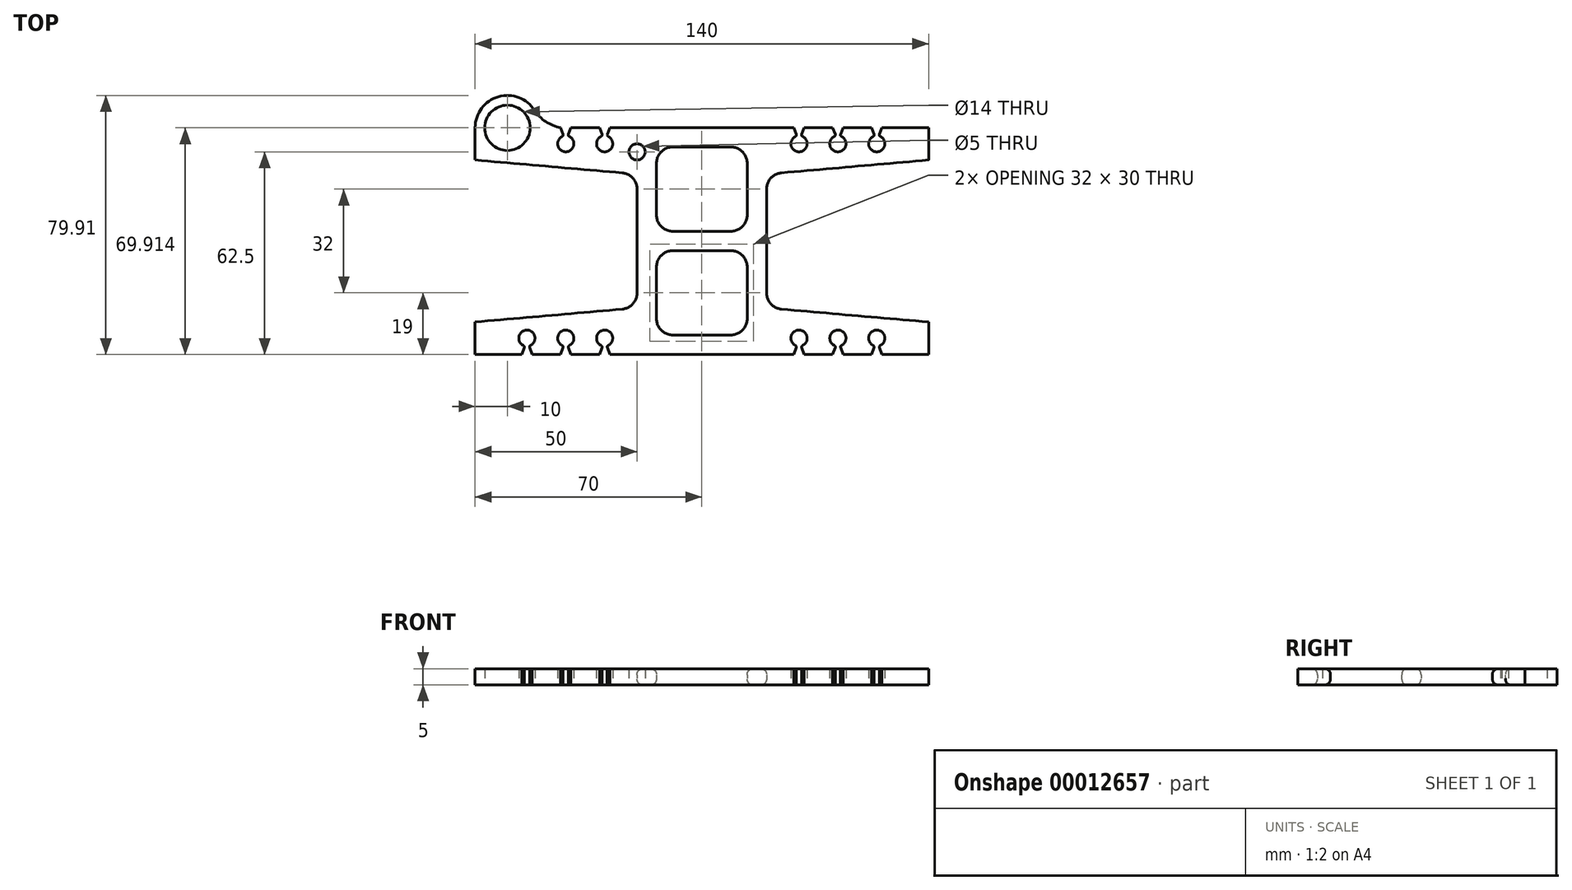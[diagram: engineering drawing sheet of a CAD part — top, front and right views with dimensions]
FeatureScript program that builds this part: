
annotation { "Feature Type Name" : "Feature", "Feature Type Description" : "" }
export const myFeature = defineFeature(function(context is Context, id is Id, definition is map)
    precondition{}
    {
        {
            var Q0;
            Q0=qCreatedBy(makeId("Top.planeOp"),FACE);
            var sketch = newSketch(context, id + "F0", { "sketchPlane" : qUnion([Q0])});
            skLineSegment(sketch, "E0", {"start": v(-20, -16.04) * mm, "end": v(-20, 16.04) * mm});
            skLineSegment(sketch, "E1", {"start": v(-24.56, 21.02) * mm, "end": v(-70, 25) * mm});
            skLineSegment(sketch, "E2", {"start": v(-70, 25) * mm, "end": v(-70, 35) * mm});
            skLineSegment(sketch, "E3", {"start": v(0, 0) * mm, "end": v(-9.78, 0) * mm, "construction": true});
            skLineSegment(sketch, "E4.0.MirrorCS", {"start": v(-70, -25) * mm, "end": v(-70, -35) * mm});
            skLineSegment(sketch, "E5", {"start": v(0, 0) * mm, "end": v(0, 8.93) * mm, "construction": true});
            skLineSegment(sketch, "E6.0.MirrorCS", {"start": v(70, 25) * mm, "end": v(70, 35) * mm});
            skLineSegment(sketch, "E7.0.MirrorCS", {"start": v(70, -25) * mm, "end": v(70, -35) * mm});
            skLineSegment(sketch, "E8", {"start": v(-70, 35) * mm, "end": v(70, 35) * mm});
            skLineSegment(sketch, "E9", {"start": v(-70, -35) * mm, "end": v(70, -35) * mm});
            skPoint(sketch, "E10.visualSharp", {"position": v(-20, 0) * mm});
            skPoint(sketch, "E11.visualSharp", {"position": v(-20, 20.63) * mm});
            skArc(sketch, "E11.filletArc", {"start": v(-20, 16.04) * mm, "mid": v(-21.31, 19.42) * mm, "end": v(-24.56, 21.02) * mm});
            skLineSegment(sketch, "E12.0.MirrorCS", {"start": v(-20, 16.04) * mm, "end": v(-20, -16.04) * mm});
            skArc(sketch, "E13.0.MirrorCS", {"start": v(-20, -16.04) * mm, "mid": v(-21.31, -19.42) * mm, "end": v(-24.56, -21.02) * mm});
            skLineSegment(sketch, "E14.0.MirrorCS", {"start": v(-24.56, -21.02) * mm, "end": v(-70, -25) * mm});
            skLineSegment(sketch, "E15.0.MirrorCS", {"start": v(24.56, 21.02) * mm, "end": v(70, 25) * mm});
            skArc(sketch, "E16.0.MirrorCS", {"start": v(20, 16.04) * mm, "mid": v(21.31, 19.42) * mm, "end": v(24.56, 21.02) * mm});
            skLineSegment(sketch, "E17.0.MirrorCS", {"start": v(20, -16.04) * mm, "end": v(20, 16.04) * mm});
            skLineSegment(sketch, "E18.0.MirrorCS", {"start": v(20, 16.04) * mm, "end": v(20, -16.04) * mm});
            skArc(sketch, "E19.0.MirrorCS", {"start": v(20, -16.04) * mm, "mid": v(21.31, -19.42) * mm, "end": v(24.56, -21.02) * mm});
            skLineSegment(sketch, "E20.0.MirrorCS", {"start": v(24.56, -21.02) * mm, "end": v(70, -25) * mm});
            skLineSegment(sketch, "E21", {"start": v(-14, 8) * mm, "end": v(-14, 24) * mm});
            skLineSegment(sketch, "E22", {"start": v(-9, 29) * mm, "end": v(9, 29) * mm});
            skLineSegment(sketch, "E23.0.MirrorCS", {"start": v(14, 8) * mm, "end": v(14, 24) * mm});
            skLineSegment(sketch, "E24.0.MirrorCS", {"start": v(-14, -8) * mm, "end": v(-14, -24) * mm});
            skLineSegment(sketch, "E25.0.MirrorCS", {"start": v(-9, -29) * mm, "end": v(9, -29) * mm});
            skLineSegment(sketch, "E26.0.MirrorCS", {"start": v(14, -8) * mm, "end": v(14, -24) * mm});
            skPoint(sketch, "E27.visualSharp", {"position": v(-14, 29) * mm});
            skArc(sketch, "E27.filletArc", {"start": v(-9, 29) * mm, "mid": v(-12.54, 27.54) * mm, "end": v(-14, 24) * mm});
            skPoint(sketch, "E28.visualSharp", {"position": v(14, 29) * mm});
            skArc(sketch, "E28.filletArc", {"start": v(14, 24) * mm, "mid": v(12.54, 27.54) * mm, "end": v(9, 29) * mm});
            skPoint(sketch, "E29.visualSharp", {"position": v(-14, -29) * mm});
            skArc(sketch, "E29.filletArc", {"start": v(-14, -24) * mm, "mid": v(-12.54, -27.54) * mm, "end": v(-9, -29) * mm});
            skPoint(sketch, "E30.visualSharp", {"position": v(14, -29) * mm});
            skArc(sketch, "E30.filletArc", {"start": v(9, -29) * mm, "mid": v(12.54, -27.54) * mm, "end": v(14, -24) * mm});
            skLineSegment(sketch, "E31", {"start": v(-9, 3) * mm, "end": v(9, 3) * mm});
            skLineSegment(sketch, "E32.0.MirrorCS", {"start": v(-9, -3) * mm, "end": v(9, -3) * mm});
            skPoint(sketch, "E33.orphan", {"position": v(-14, 0) * mm});
            skPoint(sketch, "E34.orphan", {"position": v(14, 0) * mm});
            skPoint(sketch, "E35.visualSharp", {"position": v(-14, 3) * mm});
            skArc(sketch, "E35.filletArc", {"start": v(-14, 8) * mm, "mid": v(-12.54, 4.46) * mm, "end": v(-9, 3) * mm});
            skPoint(sketch, "E36.visualSharp", {"position": v(14, 3) * mm});
            skArc(sketch, "E36.filletArc", {"start": v(9, 3) * mm, "mid": v(12.54, 4.46) * mm, "end": v(14, 8) * mm});
            skPoint(sketch, "E37.visualSharp", {"position": v(-14, -3) * mm});
            skArc(sketch, "E37.filletArc", {"start": v(-9, -3) * mm, "mid": v(-12.54, -4.46) * mm, "end": v(-14, -8) * mm});
            skPoint(sketch, "E38.visualSharp", {"position": v(14, -3) * mm});
            skArc(sketch, "E38.filletArc", {"start": v(14, -8) * mm, "mid": v(12.54, -4.46) * mm, "end": v(9, -3) * mm});
            skSolve(sketch);
        }
        {
            var Q0;
            Q0 = qSketchRegion(id + "F0", true);
            extrude(context, id + "F1", {"entities" : qUnion([Q0]), "depth" : 5 * mm});
        }
        {
            var Q0;
            Q0=qCreatedBy(makeId("Top.planeOp"),FACE);
            var sketch = newSketch(context, id + "F2", { "sketchPlane" : qUnion([Q0])});
            skLineSegment(sketch, "E39", {"start": v(-32.08, -36.31) * mm, "end": v(-30.83, -32.87) * mm});
            skLineSegment(sketch, "E40", {"start": v(-30, -26.33) * mm, "end": v(-30, -30) * mm, "construction": true});
            skArc(sketch, "E41", {"start": v(-30, -27.5) * mm, "mid": v(-32.44, -29.44) * mm, "end": v(-31.08, -32.25) * mm});
            skArc(sketch, "E42.filletArc", {"start": v(-30.83, -32.87) * mm, "mid": v(-30.84, -32.52) * mm, "end": v(-31.08, -32.25) * mm});
            skLineSegment(sketch, "E43.0.MirrorCS", {"start": v(-27.92, -36.31) * mm, "end": v(-29.17, -32.87) * mm});
            skArc(sketch, "E44.0.MirrorCS", {"start": v(-29.17, -32.87) * mm, "mid": v(-29.16, -32.52) * mm, "end": v(-28.92, -32.25) * mm});
            skArc(sketch, "E45.0.MirrorCS", {"start": v(-30, -27.5) * mm, "mid": v(-27.56, -29.44) * mm, "end": v(-28.92, -32.25) * mm});
            skLineSegment(sketch, "E46", {"start": v(-32.08, -36.31) * mm, "end": v(-27.92, -36.31) * mm});
            skLineSegment(sketch, "E47", {"start": v(0, 0) * mm, "end": v(0, -10.66) * mm, "construction": true});
            skArc(sketch, "E48.1.0.0", {"start": v(-42, -27.5) * mm, "mid": v(-44.44, -29.44) * mm, "end": v(-43.08, -32.25) * mm});
            skLineSegment(sketch, "E48.1.0.1", {"start": v(-44.08, -36.31) * mm, "end": v(-39.92, -36.31) * mm});
            skArc(sketch, "E48.1.0.2", {"start": v(-42, -27.5) * mm, "mid": v(-39.56, -29.44) * mm, "end": v(-40.92, -32.25) * mm});
            skLineSegment(sketch, "E48.1.0.3", {"start": v(-39.92, -36.31) * mm, "end": v(-41.17, -32.87) * mm});
            skLineSegment(sketch, "E48.1.0.4", {"start": v(-42, -26.33) * mm, "end": v(-42, -30) * mm, "construction": true});
            skLineSegment(sketch, "E48.1.0.5", {"start": v(-44.08, -36.31) * mm, "end": v(-42.83, -32.87) * mm});
            skArc(sketch, "E48.1.0.6", {"start": v(-41.17, -32.87) * mm, "mid": v(-41.16, -32.52) * mm, "end": v(-40.92, -32.25) * mm});
            skArc(sketch, "E48.1.0.7", {"start": v(-42.83, -32.87) * mm, "mid": v(-42.84, -32.52) * mm, "end": v(-43.08, -32.25) * mm});
            skArc(sketch, "E48.2.0.0", {"start": v(-54, -27.5) * mm, "mid": v(-56.44, -29.44) * mm, "end": v(-55.08, -32.25) * mm});
            skLineSegment(sketch, "E48.2.0.1", {"start": v(-56.08, -36.31) * mm, "end": v(-51.92, -36.31) * mm});
            skArc(sketch, "E48.2.0.2", {"start": v(-54, -27.5) * mm, "mid": v(-51.56, -29.44) * mm, "end": v(-52.92, -32.25) * mm});
            skLineSegment(sketch, "E48.2.0.3", {"start": v(-51.92, -36.31) * mm, "end": v(-53.17, -32.87) * mm});
            skLineSegment(sketch, "E48.2.0.4", {"start": v(-54, -26.33) * mm, "end": v(-54, -30) * mm, "construction": true});
            skLineSegment(sketch, "E48.2.0.5", {"start": v(-56.08, -36.31) * mm, "end": v(-54.83, -32.87) * mm});
            skArc(sketch, "E48.2.0.6", {"start": v(-53.17, -32.87) * mm, "mid": v(-53.16, -32.52) * mm, "end": v(-52.92, -32.25) * mm});
            skArc(sketch, "E48.2.0.7", {"start": v(-54.83, -32.87) * mm, "mid": v(-54.84, -32.52) * mm, "end": v(-55.08, -32.25) * mm});
            skLineSegment(sketch, "E48.direction1", {"start": v(-31.08, -32.25) * mm, "end": v(-43.08, -32.25) * mm, "construction": true});
            skLineSegment(sketch, "E49", {"start": v(0, 0) * mm, "end": v(8.83, 0) * mm, "construction": true});
            skArc(sketch, "E50.0.MirrorCS", {"start": v(30.83, -32.87) * mm, "mid": v(30.84, -32.52) * mm, "end": v(31.08, -32.25) * mm});
            skArc(sketch, "E50.1.MirrorCS", {"start": v(41.17, -32.87) * mm, "mid": v(41.16, -32.52) * mm, "end": v(40.92, -32.25) * mm});
            skArc(sketch, "E50.2.MirrorCS", {"start": v(53.17, -32.87) * mm, "mid": v(53.16, -32.52) * mm, "end": v(52.92, -32.25) * mm});
            skArc(sketch, "E50.3.MirrorCS", {"start": v(42.83, -32.87) * mm, "mid": v(42.84, -32.52) * mm, "end": v(43.08, -32.25) * mm});
            skArc(sketch, "E50.4.MirrorCS", {"start": v(54.83, -32.87) * mm, "mid": v(54.84, -32.52) * mm, "end": v(55.08, -32.25) * mm});
            skArc(sketch, "E50.5.MirrorCS", {"start": v(29.17, -32.87) * mm, "mid": v(29.16, -32.52) * mm, "end": v(28.92, -32.25) * mm});
            skArc(sketch, "E50.6.MirrorCS", {"start": v(30, -27.5) * mm, "mid": v(32.44, -29.44) * mm, "end": v(31.08, -32.25) * mm});
            skLineSegment(sketch, "E50.7.MirrorCS", {"start": v(32.08, -36.31) * mm, "end": v(30.83, -32.87) * mm});
            skLineSegment(sketch, "E50.8.MirrorCS", {"start": v(30, -26.33) * mm, "end": v(30, -30) * mm, "construction": true});
            skLineSegment(sketch, "E50.9.MirrorCS", {"start": v(44.08, -36.31) * mm, "end": v(39.92, -36.31) * mm});
            skArc(sketch, "E50.10.MirrorCS", {"start": v(30, -27.5) * mm, "mid": v(27.56, -29.44) * mm, "end": v(28.92, -32.25) * mm});
            skArc(sketch, "E50.11.MirrorCS", {"start": v(54, -27.5) * mm, "mid": v(56.44, -29.44) * mm, "end": v(55.08, -32.25) * mm});
            skLineSegment(sketch, "E50.12.MirrorCS", {"start": v(44.08, -36.31) * mm, "end": v(42.83, -32.87) * mm});
            skLineSegment(sketch, "E50.13.MirrorCS", {"start": v(42, -26.33) * mm, "end": v(42, -30) * mm, "construction": true});
            skLineSegment(sketch, "E50.14.MirrorCS", {"start": v(31.08, -32.25) * mm, "end": v(43.08, -32.25) * mm, "construction": true});
            skLineSegment(sketch, "E50.15.MirrorCS", {"start": v(54, -26.33) * mm, "end": v(54, -30) * mm, "construction": true});
            skLineSegment(sketch, "E50.16.MirrorCS", {"start": v(56.08, -36.31) * mm, "end": v(51.92, -36.31) * mm});
            skLineSegment(sketch, "E50.17.MirrorCS", {"start": v(27.92, -36.31) * mm, "end": v(29.17, -32.87) * mm});
            skLineSegment(sketch, "E50.18.MirrorCS", {"start": v(56.08, -36.31) * mm, "end": v(54.83, -32.87) * mm});
            skArc(sketch, "E50.19.MirrorCS", {"start": v(42, -27.5) * mm, "mid": v(44.44, -29.44) * mm, "end": v(43.08, -32.25) * mm});
            skArc(sketch, "E50.20.MirrorCS", {"start": v(54, -27.5) * mm, "mid": v(51.56, -29.44) * mm, "end": v(52.92, -32.25) * mm});
            skLineSegment(sketch, "E50.21.MirrorCS", {"start": v(39.92, -36.31) * mm, "end": v(41.17, -32.87) * mm});
            skLineSegment(sketch, "E50.22.MirrorCS", {"start": v(51.92, -36.31) * mm, "end": v(53.17, -32.87) * mm});
            skArc(sketch, "E50.23.MirrorCS", {"start": v(42, -27.5) * mm, "mid": v(39.56, -29.44) * mm, "end": v(40.92, -32.25) * mm});
            skLineSegment(sketch, "E50.24.MirrorCS", {"start": v(32.08, -36.31) * mm, "end": v(27.92, -36.31) * mm});
            skArc(sketch, "E51.0.MirrorCS", {"start": v(42.83, 32.87) * mm, "mid": v(42.84, 32.52) * mm, "end": v(43.08, 32.25) * mm});
            skArc(sketch, "E51.1.MirrorCS", {"start": v(30.83, 32.87) * mm, "mid": v(30.84, 32.52) * mm, "end": v(31.08, 32.25) * mm});
            skArc(sketch, "E51.2.MirrorCS", {"start": v(53.17, 32.87) * mm, "mid": v(53.16, 32.52) * mm, "end": v(52.92, 32.25) * mm});
            skArc(sketch, "E51.3.MirrorCS", {"start": v(54.83, 32.87) * mm, "mid": v(54.84, 32.52) * mm, "end": v(55.08, 32.25) * mm});
            skArc(sketch, "E51.4.MirrorCS", {"start": v(29.17, 32.87) * mm, "mid": v(29.16, 32.52) * mm, "end": v(28.92, 32.25) * mm});
            skArc(sketch, "E51.5.MirrorCS", {"start": v(41.17, 32.87) * mm, "mid": v(41.16, 32.52) * mm, "end": v(40.92, 32.25) * mm});
            skLineSegment(sketch, "E51.6.MirrorCS", {"start": v(39.92, 36.31) * mm, "end": v(41.17, 32.87) * mm});
            skLineSegment(sketch, "E51.7.MirrorCS", {"start": v(56.08, 36.31) * mm, "end": v(51.92, 36.31) * mm});
            skLineSegment(sketch, "E51.8.MirrorCS", {"start": v(44.08, 36.31) * mm, "end": v(42.83, 32.87) * mm});
            skArc(sketch, "E51.9.MirrorCS", {"start": v(30, 27.5) * mm, "mid": v(32.44, 29.44) * mm, "end": v(31.08, 32.25) * mm});
            skLineSegment(sketch, "E51.10.MirrorCS", {"start": v(56.08, 36.31) * mm, "end": v(54.83, 32.87) * mm});
            skArc(sketch, "E51.11.MirrorCS", {"start": v(54, 27.5) * mm, "mid": v(56.44, 29.44) * mm, "end": v(55.08, 32.25) * mm});
            skLineSegment(sketch, "E51.12.MirrorCS", {"start": v(30, 26.33) * mm, "end": v(30, 30) * mm, "construction": true});
            skLineSegment(sketch, "E51.13.MirrorCS", {"start": v(54, 26.33) * mm, "end": v(54, 30) * mm, "construction": true});
            skArc(sketch, "E51.14.MirrorCS", {"start": v(42, 27.5) * mm, "mid": v(39.56, 29.44) * mm, "end": v(40.92, 32.25) * mm});
            skArc(sketch, "E51.15.MirrorCS", {"start": v(54, 27.5) * mm, "mid": v(51.56, 29.44) * mm, "end": v(52.92, 32.25) * mm});
            skArc(sketch, "E51.16.MirrorCS", {"start": v(42, 27.5) * mm, "mid": v(44.44, 29.44) * mm, "end": v(43.08, 32.25) * mm});
            skLineSegment(sketch, "E51.17.MirrorCS", {"start": v(51.92, 36.31) * mm, "end": v(53.17, 32.87) * mm});
            skLineSegment(sketch, "E51.18.MirrorCS", {"start": v(32.08, 36.31) * mm, "end": v(30.83, 32.87) * mm});
            skLineSegment(sketch, "E51.19.MirrorCS", {"start": v(27.92, 36.31) * mm, "end": v(29.17, 32.87) * mm});
            skLineSegment(sketch, "E51.20.MirrorCS", {"start": v(44.08, 36.31) * mm, "end": v(39.92, 36.31) * mm});
            skLineSegment(sketch, "E51.21.MirrorCS", {"start": v(42, 26.33) * mm, "end": v(42, 30) * mm, "construction": true});
            skLineSegment(sketch, "E51.22.MirrorCS", {"start": v(31.08, 32.25) * mm, "end": v(43.08, 32.25) * mm, "construction": true});
            skLineSegment(sketch, "E51.23.MirrorCS", {"start": v(32.08, 36.31) * mm, "end": v(27.92, 36.31) * mm});
            skArc(sketch, "E51.24.MirrorCS", {"start": v(30, 27.5) * mm, "mid": v(27.56, 29.44) * mm, "end": v(28.92, 32.25) * mm});
            skArc(sketch, "E52.0.MirrorCS", {"start": v(-30.83, 32.87) * mm, "mid": v(-30.84, 32.52) * mm, "end": v(-31.08, 32.25) * mm});
            skArc(sketch, "E52.1.MirrorCS", {"start": v(-29.17, 32.87) * mm, "mid": v(-29.16, 32.52) * mm, "end": v(-28.92, 32.25) * mm});
            skArc(sketch, "E52.2.MirrorCS", {"start": v(-42.83, 32.87) * mm, "mid": v(-42.84, 32.52) * mm, "end": v(-43.08, 32.25) * mm});
            skLineSegment(sketch, "E52.3.MirrorCS", {"start": v(-30, 26.33) * mm, "end": v(-30, 30) * mm, "construction": true});
            skLineSegment(sketch, "E52.4.MirrorCS", {"start": v(-31.08, 32.25) * mm, "end": v(-43.08, 32.25) * mm, "construction": true});
            skLineSegment(sketch, "E52.5.MirrorCS", {"start": v(-42, 26.33) * mm, "end": v(-42, 30) * mm, "construction": true});
            skArc(sketch, "E52.6.MirrorCS", {"start": v(-41.17, 32.87) * mm, "mid": v(-41.16, 32.52) * mm, "end": v(-40.92, 32.25) * mm});
            skLineSegment(sketch, "E52.7.MirrorCS", {"start": v(-32.08, 36.31) * mm, "end": v(-27.92, 36.31) * mm});
            skArc(sketch, "E52.8.MirrorCS", {"start": v(-30, 27.5) * mm, "mid": v(-32.44, 29.44) * mm, "end": v(-31.08, 32.25) * mm});
            skArc(sketch, "E52.9.MirrorCS", {"start": v(-30, 27.5) * mm, "mid": v(-27.56, 29.44) * mm, "end": v(-28.92, 32.25) * mm});
            skLineSegment(sketch, "E52.10.MirrorCS", {"start": v(-39.92, 36.31) * mm, "end": v(-41.17, 32.87) * mm});
            skLineSegment(sketch, "E52.11.MirrorCS", {"start": v(-44.08, 36.31) * mm, "end": v(-39.92, 36.31) * mm});
            skLineSegment(sketch, "E52.12.MirrorCS", {"start": v(-32.08, 36.31) * mm, "end": v(-30.83, 32.87) * mm});
            skLineSegment(sketch, "E52.13.MirrorCS", {"start": v(-27.92, 36.31) * mm, "end": v(-29.17, 32.87) * mm});
            skArc(sketch, "E52.14.MirrorCS", {"start": v(-42, 27.5) * mm, "mid": v(-39.56, 29.44) * mm, "end": v(-40.92, 32.25) * mm});
            skLineSegment(sketch, "E52.15.MirrorCS", {"start": v(-44.08, 36.31) * mm, "end": v(-42.83, 32.87) * mm});
            skArc(sketch, "E52.16.MirrorCS", {"start": v(-42, 27.5) * mm, "mid": v(-44.44, 29.44) * mm, "end": v(-43.08, 32.25) * mm});
            skSolve(sketch);
        }
        {
            var Q0;
            Q0 = qSketchRegion(id + "F2", true);
            extrude(context, id + "F3", {"entities" : qUnion([Q0]), "operationType" : NewBodyOperationType.REMOVE, "endBound" : BoundingType.THROUGH_ALL, "depth" : 25 * mm});
        }
        {
            var Q0;
            Q0=qCreatedBy(makeId("Top.planeOp"),FACE);
            var sketch = newSketch(context, id + "F4", { "sketchPlane" : qUnion([Q0])});
            skCircle(sketch, "E53", {"center": v(-60, 34.91) * mm, "radius": 10 * mm});
            skSolve(sketch);
        }
        {
            var Q0;
            Q0 = qSketchRegion(id + "F4", true);
            extrude(context, id + "F5", {"entities" : qUnion([Q0]), "operationType" : NewBodyOperationType.ADD, "depth" : 5 * mm});
        }
        {
            var Q0;
            {var subQ0=sQuery(id+"F0.wireOp",EDGE,"E8");var subQ1=sQuery(id+"F0.wireOp",EDGE,"E2");Q0=makeQuery(id+"F5.boolean.opBoolean","INTERSECT",EDGE,{"disambiguationData":[OD(1.0)],"derivedFrom":[makeQuery(id+"F3.boolean.opBoolean","SPLIT",FACE,{"disambiguationData":[TD([makeQuery(id+"F1.opExtrude","SWEPT_FACE",FACE,{"disambiguationData":[OSD([subQ1])]})])],"derivedFrom":makeQuery(id+"F1.opExtrude","SWEPT_FACE",FACE,{"disambiguationData":[OSD([subQ0])]})}),makeQuery(id+"F5.opExtrude","SWEPT_FACE",FACE,{"disambiguationData":[OSD([sQuery(id+"F4.wireOp",EDGE,"E53")])]})]});}
            fillet(context, id + "F6", {"entities" : qUnion([Q0]), "radius" : 12 * mm, "tangentPropagation" : true, "allowEdgeOverflow" : false});
        }
        {
            var Q0;
            Q0=sQuery(id+"F4.wireOp",VERTEX,"E53.center");
            var Q1;
            Q1=makeQuery(id+"F1.opExtrude","SWEPT_BODY",BODY,{"disambiguationData":[OSD([sQuery(id+"F0.wireOp",EDGE,"E1"),sQuery(id+"F0.wireOp",EDGE,"E2"),sQuery(id+"F0.wireOp",EDGE,"E4.0.MirrorCS"),sQuery(id+"F0.wireOp",EDGE,"E6.0.MirrorCS"),sQuery(id+"F0.wireOp",EDGE,"E7.0.MirrorCS"),sQuery(id+"F0.wireOp",EDGE,"E8"),sQuery(id+"F0.wireOp",EDGE,"E9"),sQuery(id+"F0.wireOp",EDGE,"E11.filletArc"),sQuery(id+"F0.wireOp",EDGE,"E12.0.MirrorCS"),sQuery(id+"F0.wireOp",EDGE,"E13.0.MirrorCS"),sQuery(id+"F0.wireOp",EDGE,"E14.0.MirrorCS"),sQuery(id+"F0.wireOp",EDGE,"E15.0.MirrorCS"),sQuery(id+"F0.wireOp",EDGE,"E16.0.MirrorCS"),sQuery(id+"F0.wireOp",EDGE,"E18.0.MirrorCS"),sQuery(id+"F0.wireOp",EDGE,"E19.0.MirrorCS"),sQuery(id+"F0.wireOp",EDGE,"E20.0.MirrorCS")])]});
            hole(context, id + "F7", {"style" : HoleStyle.SIMPLE, "holeDiameter" : 14 * mm, "endStyle" : HoleEndStyle.THROUGH, "oppositeDirection" : true, "locations" : qUnion([Q0]), "scope" : qUnion([Q1])});
        }
        {
            var Q0;
            Q0=qCreatedBy(makeId("Top.planeOp"),FACE);
            var sketch = newSketch(context, id + "F8", { "sketchPlane" : qUnion([Q0])});
            skPoint(sketch, "E54", {"position": v(-20, 27.5) * mm});
            skSolve(sketch);
        }
        {
            var Q0;
            Q0=sQuery(id+"F8.wireOp",VERTEX,"E54");
            var Q1;
            Q1=makeQuery(id+"F1.opExtrude","SWEPT_BODY",BODY,{"disambiguationData":[OSD([sQuery(id+"F0.wireOp",EDGE,"E1"),sQuery(id+"F0.wireOp",EDGE,"E2"),sQuery(id+"F0.wireOp",EDGE,"E4.0.MirrorCS"),sQuery(id+"F0.wireOp",EDGE,"E6.0.MirrorCS"),sQuery(id+"F0.wireOp",EDGE,"E7.0.MirrorCS"),sQuery(id+"F0.wireOp",EDGE,"E8"),sQuery(id+"F0.wireOp",EDGE,"E9"),sQuery(id+"F0.wireOp",EDGE,"E11.filletArc"),sQuery(id+"F0.wireOp",EDGE,"E12.0.MirrorCS"),sQuery(id+"F0.wireOp",EDGE,"E13.0.MirrorCS"),sQuery(id+"F0.wireOp",EDGE,"E14.0.MirrorCS"),sQuery(id+"F0.wireOp",EDGE,"E15.0.MirrorCS"),sQuery(id+"F0.wireOp",EDGE,"E16.0.MirrorCS"),sQuery(id+"F0.wireOp",EDGE,"E18.0.MirrorCS"),sQuery(id+"F0.wireOp",EDGE,"E19.0.MirrorCS"),sQuery(id+"F0.wireOp",EDGE,"E20.0.MirrorCS"),sQuery(id+"F0.wireOp",EDGE,"E21"),sQuery(id+"F0.wireOp",EDGE,"E22"),sQuery(id+"F0.wireOp",EDGE,"E23.0.MirrorCS"),sQuery(id+"F0.wireOp",EDGE,"E24.0.MirrorCS"),sQuery(id+"F0.wireOp",EDGE,"E25.0.MirrorCS"),sQuery(id+"F0.wireOp",EDGE,"E26.0.MirrorCS"),sQuery(id+"F0.wireOp",EDGE,"E27.filletArc"),sQuery(id+"F0.wireOp",EDGE,"E28.filletArc"),sQuery(id+"F0.wireOp",EDGE,"E29.filletArc"),sQuery(id+"F0.wireOp",EDGE,"E30.filletArc")])]});
            hole(context, id + "F9", {"style" : HoleStyle.SIMPLE, "holeDiameter" : 5 * mm, "endStyle" : HoleEndStyle.THROUGH, "oppositeDirection" : true, "locations" : qUnion([Q0]), "scope" : qUnion([Q1])});
        }
        {
            var Q0;
            Q0=makeQuery(id+"F1.opExtrude","CAP_EDGE",EDGE,{"disambiguationData":[OSD([sQuery(id+"F0.wireOp",EDGE,"E22")])],"isStart":false});
            var Q1;
            Q1=makeQuery(id+"F1.opExtrude","CAP_EDGE",EDGE,{"disambiguationData":[OSD([sQuery(id+"F0.wireOp",EDGE,"E22")])],"isStart":true});
            var Q2;
            Q2=makeQuery(id+"F1.opExtrude","CAP_EDGE",EDGE,{"disambiguationData":[OSD([sQuery(id+"F0.wireOp",EDGE,"E11.filletArc")])],"isStart":false});
            var Q3;
            Q3=makeQuery(id+"F1.opExtrude","CAP_EDGE",EDGE,{"disambiguationData":[OSD([sQuery(id+"F0.wireOp",EDGE,"E11.filletArc")])],"isStart":true});
            var Q4;
            Q4=makeQuery(id+"F1.opExtrude","CAP_EDGE",EDGE,{"disambiguationData":[OSD([sQuery(id+"F0.wireOp",EDGE,"E15.0.MirrorCS")])],"isStart":false});
            var Q5;
            Q5=makeQuery(id+"F1.opExtrude","CAP_EDGE",EDGE,{"disambiguationData":[OSD([sQuery(id+"F0.wireOp",EDGE,"E15.0.MirrorCS")])],"isStart":true});
            var Q6;
            Q6=makeQuery(id+"F1.opExtrude","CAP_EDGE",EDGE,{"disambiguationData":[OSD([sQuery(id+"F0.wireOp",EDGE,"E32.0.MirrorCS")])],"isStart":false});
            var Q7;
            Q7=makeQuery(id+"F1.opExtrude","CAP_EDGE",EDGE,{"disambiguationData":[OSD([sQuery(id+"F0.wireOp",EDGE,"E32.0.MirrorCS")])],"isStart":true});
            fillet(context, id + "F10", {"entities" : qUnion([Q0, Q1, Q2, Q3, Q4, Q5, Q6, Q7]), "radius" : 2 * mm, "tangentPropagation" : true, "rho" : 0.5, "crossSection" : FilletCrossSection.CONIC, "allowEdgeOverflow" : false});
        }
    });
